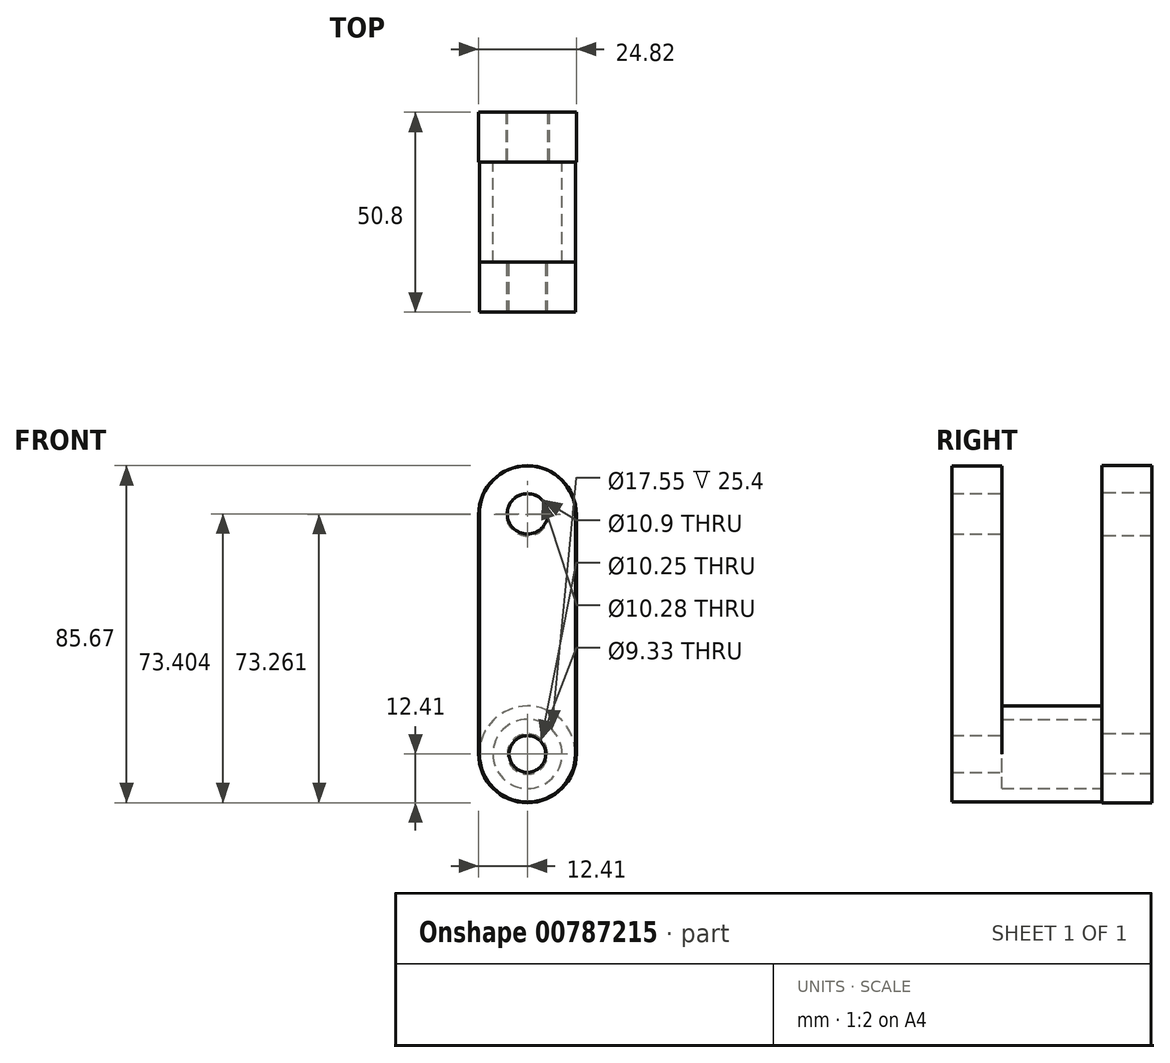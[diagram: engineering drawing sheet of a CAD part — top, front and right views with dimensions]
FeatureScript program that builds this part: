
annotation { "Feature Type Name" : "Feature", "Feature Type Description" : "" }
export const myFeature = defineFeature(function(context is Context, id is Id, definition is map)
    precondition{}
    {
        {
            var Q0;
            Q0=qCreatedBy(makeId("Front.planeOp"),FACE);
            var sketch = newSketch(context, id + "F0", { "sketchPlane" : qUnion([Q0])});
            skCircle(sketch, "E0", {"center": v(0, 0) * mm, "radius": 8.78 * mm});
            skCircle(sketch, "E1", {"center": v(0, 0) * mm, "radius": 12.19 * mm});
            skSolve(sketch);
        }
        {
            var Q0;
            Q0=makeQuery(id+"F0.imprint","IMPRINT",FACE,{"disambiguationData":[TD([[makeQuery(id+"F0.imprint","IMPRINT",EDGE,{"derivedFrom":sQuery(id+"F0.wireOp",EDGE,"E0")}),-1.0]])]});
            extrude(context, id + "F1", {"entities" : qUnion([Q0]), "depth" : 25.4 * mm, "offsetDistance" : 25.4 * mm});
        }
        {
            var Q0;
            Q0=qCreatedBy(makeId("Front.planeOp"),FACE);
            var sketch = newSketch(context, id + "F2", { "sketchPlane" : qUnion([Q0])});
            skLineSegment(sketch, "E2", {"start": v(-12.41, 0) * mm, "end": v(-12.41, 60.85) * mm});
            skLineSegment(sketch, "E3", {"start": v(12.41, 0) * mm, "end": v(12.41, 60.85) * mm});
            skArc(sketch, "E4", {"start": v(12.41, 60.85) * mm, "mid": v(0, 73.26) * mm, "end": v(-12.41, 60.85) * mm});
            skCircle(sketch, "E5", {"center": v(0, 60.85) * mm, "radius": 5.45 * mm});
            skCircle(sketch, "E6", {"center": v(0, 0) * mm, "radius": 5.13 * mm});
            skArc(sketch, "E7", {"start": v(-12.41, 0) * mm, "mid": v(0, -12.41) * mm, "end": v(12.41, 0) * mm});
            skSolve(sketch);
        }
        {
            var Q0;
            Q0 = qSketchRegion(id + "F2", true);
            extrude(context, id + "F3", {"entities" : qUnion([Q0]), "operationType" : NewBodyOperationType.ADD, "depth" : -12.7 * mm, "offsetDistance" : 25.4 * mm});
        }
        {
            var Q0;
            Q0=makeQuery(id+"F1.opExtrude","CAP_FACE",FACE,{"disambiguationData":[OSD([sQuery(id+"F0.wireOp",EDGE,"E0"),sQuery(id+"F0.wireOp",EDGE,"E1")])],"isStart":false});
            var sketch = newSketch(context, id + "F4", { "sketchPlane" : qUnion([Q0])});
            skLineSegment(sketch, "E8", {"start": v(-12.19, 0) * mm, "end": v(-12.19, 61) * mm});
            skLineSegment(sketch, "E9", {"start": v(12.19, 0) * mm, "end": v(12.19, 61) * mm});
            skArc(sketch, "E10", {"start": v(12.19, 61) * mm, "mid": v(0, 73.18) * mm, "end": v(-12.19, 61) * mm});
            skArc(sketch, "E11", {"start": v(-12.19, 0) * mm, "mid": v(0, -12.19) * mm, "end": v(12.19, 0) * mm});
            skCircle(sketch, "E12", {"center": v(0, 61) * mm, "radius": 5.14 * mm});
            skCircle(sketch, "E13", {"center": v(0, 0) * mm, "radius": 4.66 * mm});
            skSolve(sketch);
        }
        {
            var Q0;
            Q0 = qSketchRegion(id + "F4", true);
            extrude(context, id + "F5", {"entities" : qUnion([Q0]), "operationType" : NewBodyOperationType.ADD, "depth" : 12.7 * mm, "offsetDistance" : 25.4 * mm});
        }
    });
